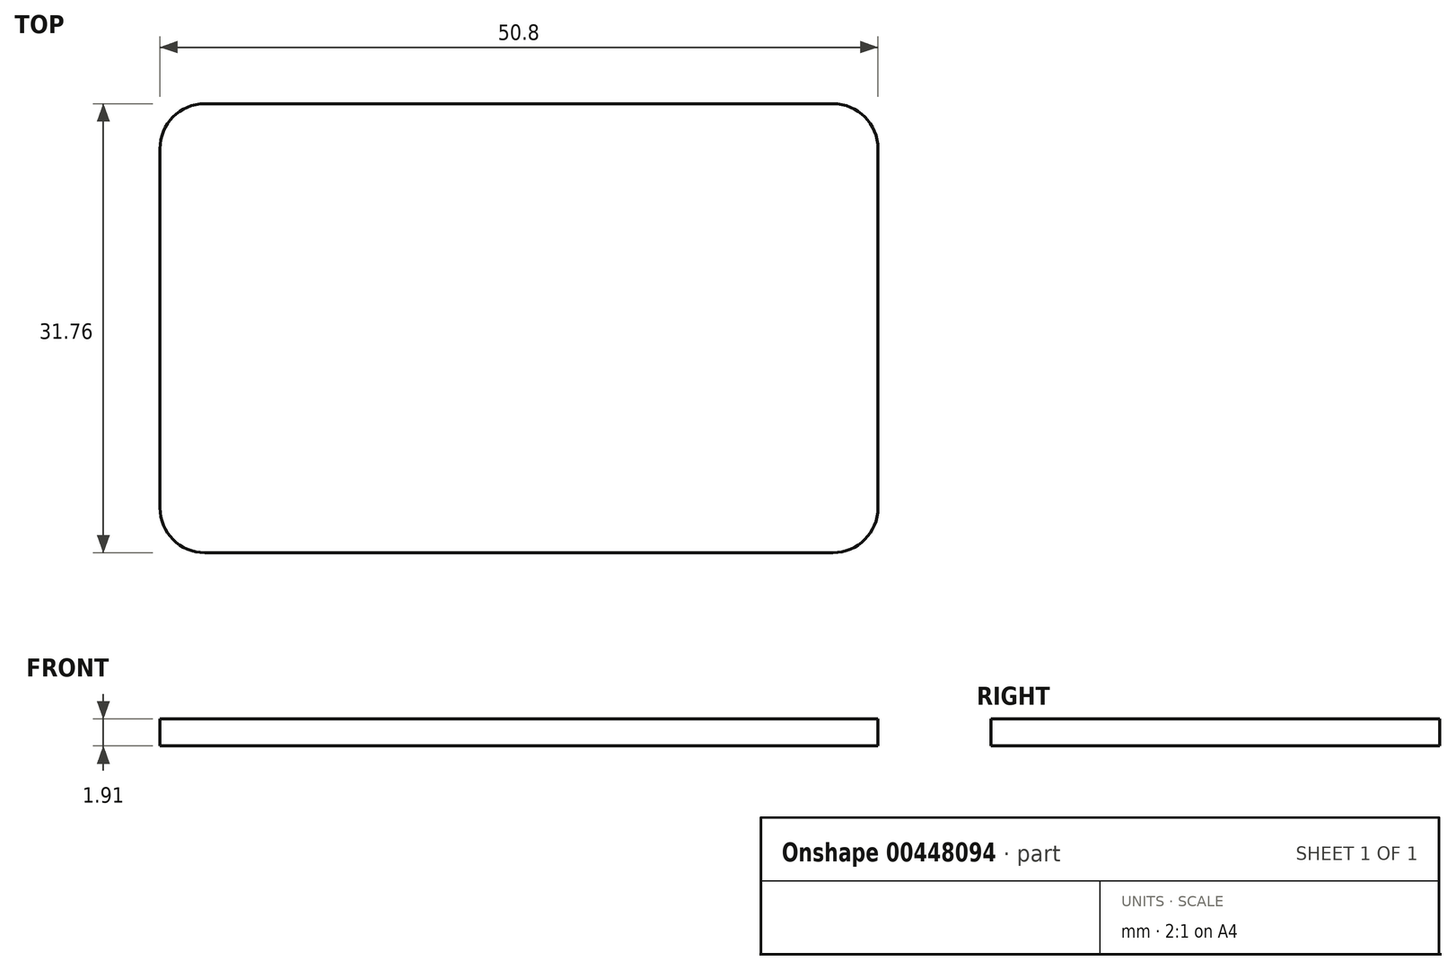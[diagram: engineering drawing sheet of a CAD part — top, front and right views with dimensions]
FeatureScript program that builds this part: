
annotation { "Feature Type Name" : "Feature", "Feature Type Description" : "" }
export const myFeature = defineFeature(function(context is Context, id is Id, definition is map)
    precondition{}
    {
        {
            var Q0;
            Q0=qCreatedBy(makeId("Top.planeOp"),FACE);
            var sketch = newSketch(context, id + "F0", { "sketchPlane" : qUnion([Q0])});
            skLineSegment(sketch, "E0.bottom", {"start": v(22.23, -15.88) * mm, "end": v(-22.23, -15.88) * mm});
            skLineSegment(sketch, "E0.top", {"start": v(22.23, 15.88) * mm, "end": v(-22.23, 15.88) * mm});
            skLineSegment(sketch, "E0.left", {"start": v(25.4, -12.7) * mm, "end": v(25.4, 12.7) * mm});
            skLineSegment(sketch, "E0.right", {"start": v(-25.4, -12.7) * mm, "end": v(-25.4, 12.7) * mm});
            skPoint(sketch, "E0.middle", {"position": v(0, 0) * mm});
            skPoint(sketch, "E1.visualSharp", {"position": v(-25.4, 15.88) * mm});
            skArc(sketch, "E1.filletArc", {"start": v(-22.23, 15.87) * mm, "mid": v(-24.47, 14.95) * mm, "end": v(-25.4, 12.7) * mm});
            skPoint(sketch, "E2.visualSharp", {"position": v(-25.4, -15.88) * mm});
            skArc(sketch, "E2.filletArc", {"start": v(-25.4, -12.7) * mm, "mid": v(-24.47, -14.95) * mm, "end": v(-22.23, -15.88) * mm});
            skPoint(sketch, "E3.visualSharp", {"position": v(25.4, -15.88) * mm});
            skArc(sketch, "E3.filletArc", {"start": v(22.23, -15.88) * mm, "mid": v(24.47, -14.95) * mm, "end": v(25.4, -12.7) * mm});
            skPoint(sketch, "E4.visualSharp", {"position": v(25.4, 15.88) * mm});
            skArc(sketch, "E4.filletArc", {"start": v(25.4, 12.7) * mm, "mid": v(24.47, 14.95) * mm, "end": v(22.23, 15.88) * mm});
            skSolve(sketch);
        }
        {
            var Q0;
            Q0 = qSketchRegion(id + "F0", true);
            extrude(context, id + "F1", {"entities" : qUnion([Q0]), "depth" : 1.9 * mm});
        }
    });
